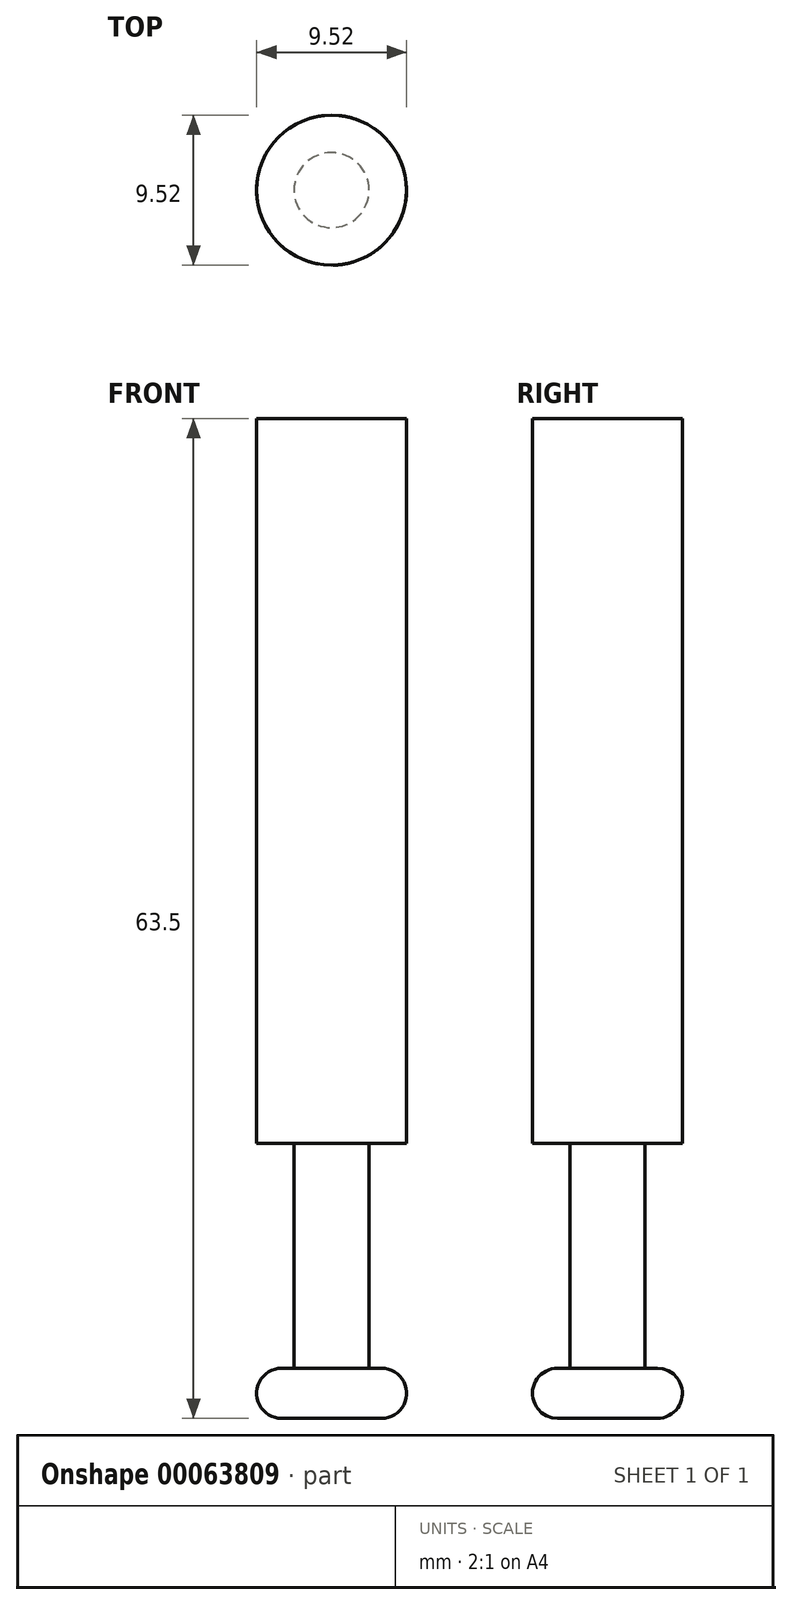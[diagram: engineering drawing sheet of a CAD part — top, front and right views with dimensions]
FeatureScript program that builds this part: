
annotation { "Feature Type Name" : "Feature", "Feature Type Description" : "" }
export const myFeature = defineFeature(function(context is Context, id is Id, definition is map)
    precondition{}
    {
        {
            var Q0;
            Q0=qCreatedBy(makeId("Front.planeOp"),FACE);
            var sketch = newSketch(context, id + "F0", { "sketchPlane" : qUnion([Q0])});
            skLineSegment(sketch, "E0", {"start": v(-4.76, 63.5) * mm, "end": v(-4.76, 17.46) * mm});
            skLineSegment(sketch, "E1", {"start": v(-4.76, 17.46) * mm, "end": v(-2.38, 17.46) * mm});
            skLineSegment(sketch, "E2", {"start": v(-2.38, 17.46) * mm, "end": v(-2.38, 3.18) * mm});
            skLineSegment(sketch, "E3", {"start": v(-2.38, 3.17) * mm, "end": v(-3.17, 3.17) * mm});
            skArc(sketch, "E4", {"start": v(-3.18, 3.17) * mm, "mid": v(-4.76, 1.59) * mm, "end": v(-3.17, 0) * mm});
            skLineSegment(sketch, "E5", {"start": v(-3.17, 0) * mm, "end": v(0, 0) * mm});
            skLineSegment(sketch, "E6", {"start": v(0, 0) * mm, "end": v(0, 63.5) * mm});
            skLineSegment(sketch, "E7", {"start": v(-4.76, 63.5) * mm, "end": v(0, 63.5) * mm});
            skLineSegment(sketch, "E8.MirrorCS", {"start": v(3.17, 0) * mm, "end": v(0, 0) * mm, "construction": true});
            skArc(sketch, "E9.MirrorCS", {"start": v(3.18, 3.17) * mm, "mid": v(4.76, 1.59) * mm, "end": v(3.17, 0) * mm, "construction": true});
            skLineSegment(sketch, "E10.MirrorCS", {"start": v(2.38, 3.17) * mm, "end": v(3.17, 3.17) * mm, "construction": true});
            skLineSegment(sketch, "E11.MirrorCS", {"start": v(2.38, 17.46) * mm, "end": v(2.38, 3.18) * mm, "construction": true});
            skLineSegment(sketch, "E12.MirrorCS", {"start": v(4.76, 17.46) * mm, "end": v(2.38, 17.46) * mm, "construction": true});
            skLineSegment(sketch, "E13.MirrorCS", {"start": v(4.76, 63.5) * mm, "end": v(4.76, 17.46) * mm, "construction": true});
            skSolve(sketch);
        }
        {
            var Q0;
            Q0 = qSketchRegion(id + "F0", true);
            var Q1;
            Q1=sQuery(id+"F0.wireOp",EDGE,"E6");
            revolve(context, id + "F1", {"entities" : qUnion([Q0]), "axis" : qUnion([Q1]), "revolveType" : RevolveType.FULL});
        }
    });
